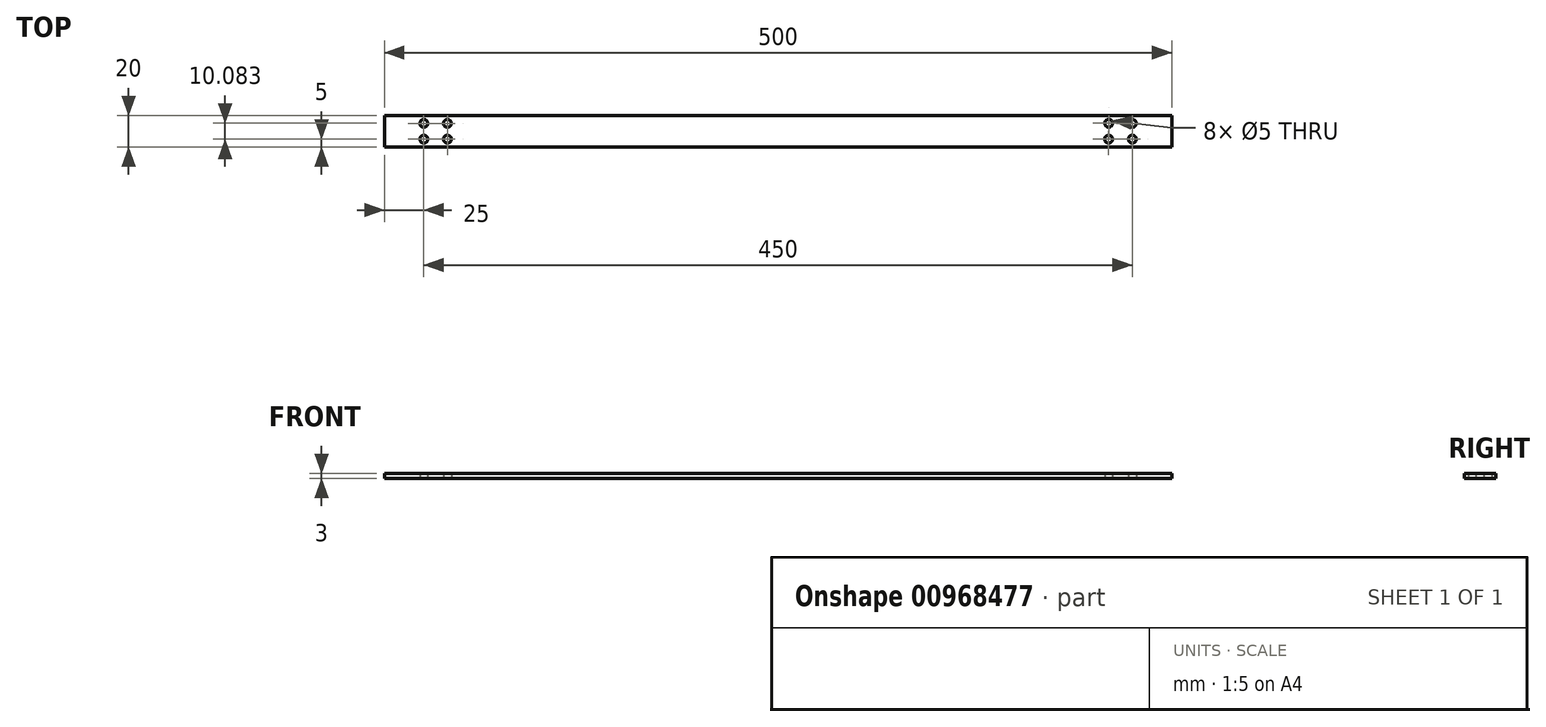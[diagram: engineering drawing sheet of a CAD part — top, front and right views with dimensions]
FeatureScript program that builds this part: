
annotation { "Feature Type Name" : "Feature", "Feature Type Description" : "" }
export const myFeature = defineFeature(function(context is Context, id is Id, definition is map)
    precondition{}
    {
        {
            var Q0;
            Q0=qCreatedBy(makeId("Top.planeOp"),FACE);
            var sketch = newSketch(context, id + "F0", { "sketchPlane" : qUnion([Q0])});
            skLineSegment(sketch, "E0.bottom", {"start": v(250, 10) * mm, "end": v(-250, 10) * mm});
            skLineSegment(sketch, "E0.top", {"start": v(250, -10) * mm, "end": v(-250, -10) * mm});
            skLineSegment(sketch, "E0.left", {"start": v(250, 10) * mm, "end": v(250, -10) * mm});
            skLineSegment(sketch, "E0.right", {"start": v(-250, 10) * mm, "end": v(-250, -10) * mm});
            skPoint(sketch, "E0.middle", {"position": v(0, 0) * mm});
            skLineSegment(sketch, "E1", {"start": v(-225, 22.28) * mm, "end": v(-225, -23.47) * mm, "construction": true});
            skLineSegment(sketch, "E2", {"start": v(225, 23.35) * mm, "end": v(225, -23.47) * mm, "construction": true});
            skCircle(sketch, "E3", {"center": v(-225, 5) * mm, "radius": 2.5 * mm});
            skCircle(sketch, "E4", {"center": v(-225, -5) * mm, "radius": 2.5 * mm});
            skCircle(sketch, "E5", {"center": v(225, 5) * mm, "radius": 2.5 * mm});
            skCircle(sketch, "E6", {"center": v(225, -5) * mm, "radius": 2.5 * mm});
            skCircle(sketch, "E7", {"center": v(-210, 5) * mm, "radius": 2.5 * mm});
            skCircle(sketch, "E8", {"center": v(-210, -5) * mm, "radius": 2.5 * mm});
            skLineSegment(sketch, "E9", {"start": v(-225, 5) * mm, "end": v(-210, 5) * mm, "construction": true});
            skLineSegment(sketch, "E10", {"start": v(-210, -5) * mm, "end": v(-225, -5) * mm, "construction": true});
            skLineSegment(sketch, "E11", {"start": v(-210, -5) * mm, "end": v(-210, 5) * mm, "construction": true});
            skLineSegment(sketch, "E12", {"start": v(225, 5) * mm, "end": v(210, 5.08) * mm, "construction": true});
            skLineSegment(sketch, "E13", {"start": v(210, 5.08) * mm, "end": v(209.94, -5) * mm, "construction": true});
            skLineSegment(sketch, "E14", {"start": v(209.94, -5) * mm, "end": v(225, -5) * mm, "construction": true});
            skCircle(sketch, "E15", {"center": v(210, 5.08) * mm, "radius": 2.5 * mm});
            skCircle(sketch, "E16", {"center": v(209.94, -5) * mm, "radius": 2.5 * mm});
            skSolve(sketch);
        }
        {
            var Q0;
            Q0=makeQuery(id+"F0.imprint","IMPRINT",FACE,{"disambiguationData":[TD([[makeQuery(id+"F0.imprint","IMPRINT",EDGE,{"derivedFrom":sQuery(id+"F0.wireOp",EDGE,"E0.bottom")}),1.0]])]});
            extrude(context, id + "F1", {"entities" : qUnion([Q0]), "depth" : 3 * mm, "offsetDistance" : 25 * mm});
        }
    });
